# Revit family: Oventrop Hydrocontrol MTR Strangregulierventil IG-IG mit Messventilen
name_source: partatom
category: Pipe Accessories
revit_build: Autodesk Revit MEP 2012 (Build: 20110309_2315(x64)
units: mm (PartAtom-declared; Revit-internal decimal feet)

## types (8) — shared parameters
Angle = 50.00°
Angle 2 = 60.00°
Hb4 = 18 mm  [stored 0.0590551 ft]
Hb5 = 3 mm  [stored 0.00984252 ft]
Hlp1 = 22 mm  [stored 0.0721785 ft]
Lgt2 = 11 mm  [stored 0.0360892 ft]
Manufacturer = Oventrop GmbH & Co. KG
Pressure Drop = 0.0 Pa
R1 = 9 mm  [stored 0.0295276 ft]
r1 = 2 mm  [stored 0.00656168 ft]
r2 = 3 mm  [stored 0.00984252 ft]

## per-type parameters (varying)
| type | D | Description | H | Hb1 | Hb2 | Hb3 | Hb6 | Hb7 | Hb8 | L1 | L2 | Lgt1 | Lgt3 | Lgt4 | Nominal Diameter | Nominal Radius | Rad1 | Rad2 | Rad3 | Rad4 | Rad5 | SW | SW2 | t |
| ND 40 | 45 mm  [stored 0.147638 ft] | 1060412 | 138 mm | 151 mm | 50 mm | 5 mm  [stored 0.0164042 ft] | 44 mm | 74 mm | 47 mm | 132 mm | 10 mm  [stored 0.0328084 ft] | 21 mm | 87 mm | 16 mm  [stored 0.0524934 ft] | 40 mm | 20 mm | 23 mm  [stored 0.0754593 ft] | 21 mm | 23 mm  [stored 0.0754593 ft] | 26 mm | 28 mm | 56 mm | 65 mm | 19 mm  [stored 0.062336 ft] |
| ND 50 | 57 mm | 1060416 | 148 mm | 164 mm | 50 mm | 15 mm  [stored 0.0492126 ft] | 52 mm | 86 mm | 56 mm | 163 mm | 12 mm  [stored 0.0393701 ft] | 28 mm | 107 mm | 20 mm  [stored 0.0656168 ft] | 50 mm | 25 mm | 29 mm | 27 mm  [stored 0.0885827 ft] | 29 mm | 32 mm  [stored 0.104987 ft] | 34 mm | 70 mm | 80 mm | 26 mm |
| ND 32 | 39 mm  [stored 0.127953 ft] | 1060410 | 136 mm | 148 mm | 50 mm | 1 mm  [stored 0.00328084 ft] | 40 mm  [stored 0.131234 ft] | 68 mm | 42 mm  [stored 0.137795 ft] | 119 mm | 8 mm  [stored 0.0262467 ft] | 21 mm | 82 mm | 13 mm | 32 mm | 16 mm | 20 mm  [stored 0.0656168 ft] | 18 mm  [stored 0.0590551 ft] | 20 mm  [stored 0.0656168 ft] | 23 mm  [stored 0.0754593 ft] | 25 mm  [stored 0.082021 ft] | 49 mm | 57 mm | 19 mm  [stored 0.062336 ft] |
| ND 25 | 31 mm  [stored 0.101706 ft] | 1060408 | 119 mm | 126 mm | 25 mm  [stored 0.082021 ft] | 13 mm | 35 mm  [stored 0.114829 ft] | 53 mm | 36 mm | 102 mm | 6 mm  [stored 0.019685 ft] | 19 mm  [stored 0.062336 ft] | 67 mm | 10 mm  [stored 0.0328084 ft] | 25 mm | 13 mm | 16 mm  [stored 0.0524934 ft] | 14 mm  [stored 0.0459318 ft] | 16 mm  [stored 0.0524934 ft] | 19 mm  [stored 0.062336 ft] | 21 mm | 40 mm  [stored 0.131234 ft] | 46 mm | 17 mm  [stored 0.0557743 ft] |
| ND 20 | 24 mm  [stored 0.0787402 ft] | 1060406 | 116 mm | 122 mm | 22 mm  [stored 0.0721785 ft] | 11 mm  [stored 0.0360892 ft] | 35 mm  [stored 0.114829 ft] | 47 mm | 36 mm | 96 mm | 5 mm  [stored 0.0164042 ft] | 17 mm  [stored 0.0557743 ft] | 58 mm | 10 mm  [stored 0.0328084 ft] | 20 mm | 10 mm | 12 mm  [stored 0.0393701 ft] | 10 mm  [stored 0.0328084 ft] | 13 mm | 15 mm  [stored 0.0492126 ft] | 17 mm  [stored 0.0557743 ft] | 32 mm  [stored 0.104987 ft] | 37 mm | 15 mm  [stored 0.0492126 ft] |
| ND 15 | 20 mm  [stored 0.0656168 ft] | 1060404 | 114 mm | 119 mm | 19 mm  [stored 0.062336 ft] | 15 mm  [stored 0.0492126 ft] | 35 mm  [stored 0.114829 ft] | 47 mm | 36 mm | 87 mm | 4 mm  [stored 0.0131234 ft] | 15 mm  [stored 0.0492126 ft] | 55 mm | 10 mm  [stored 0.0328084 ft] | 15 mm | 8 mm | 10 mm  [stored 0.0328084 ft] | 8 mm  [stored 0.0262467 ft] | 11 mm  [stored 0.0360892 ft] | 13 mm | 15 mm  [stored 0.0492126 ft] | 27 mm  [stored 0.0885827 ft] | 32 mm  [stored 0.104987 ft] | 13 mm |
| ND 15 MF | 20 mm  [stored 0.0656168 ft] | 1060434 | 114 mm | 119 mm | 19 mm  [stored 0.062336 ft] | 15 mm  [stored 0.0492126 ft] | 35 mm  [stored 0.114829 ft] | 47 mm | 36 mm | 87 mm | 4 mm  [stored 0.0131234 ft] | 15 mm  [stored 0.0492126 ft] | 55 mm | 10 mm  [stored 0.0328084 ft] | 15 mm | 8 mm | 10 mm  [stored 0.0328084 ft] | 8 mm  [stored 0.0262467 ft] | 11 mm  [stored 0.0360892 ft] | 13 mm | 15 mm  [stored 0.0492126 ft] | 27 mm  [stored 0.0885827 ft] | 32 mm  [stored 0.104987 ft] | 13 mm |
| ND 15 LF | 20 mm  [stored 0.0656168 ft] | 1060464 | 114 mm | 119 mm | 19 mm  [stored 0.062336 ft] | 15 mm  [stored 0.0492126 ft] | 35 mm  [stored 0.114829 ft] | 47 mm | 36 mm | 87 mm | 4 mm  [stored 0.0131234 ft] | 15 mm  [stored 0.0492126 ft] | 55 mm | 10 mm  [stored 0.0328084 ft] | 15 mm | 8 mm | 10 mm  [stored 0.0328084 ft] | 8 mm  [stored 0.0262467 ft] | 11 mm  [stored 0.0360892 ft] | 13 mm | 15 mm  [stored 0.0492126 ft] | 27 mm  [stored 0.0885827 ft] | 32 mm  [stored 0.104987 ft] | 13 mm |

note: [stored X ft] marks values corroborated as IEEE doubles in the binary element streams (Revit-internal decimal feet)

## geometry (parser evidence)
native form markers: Sweep x1
no freeform markers — native parametric forms only
